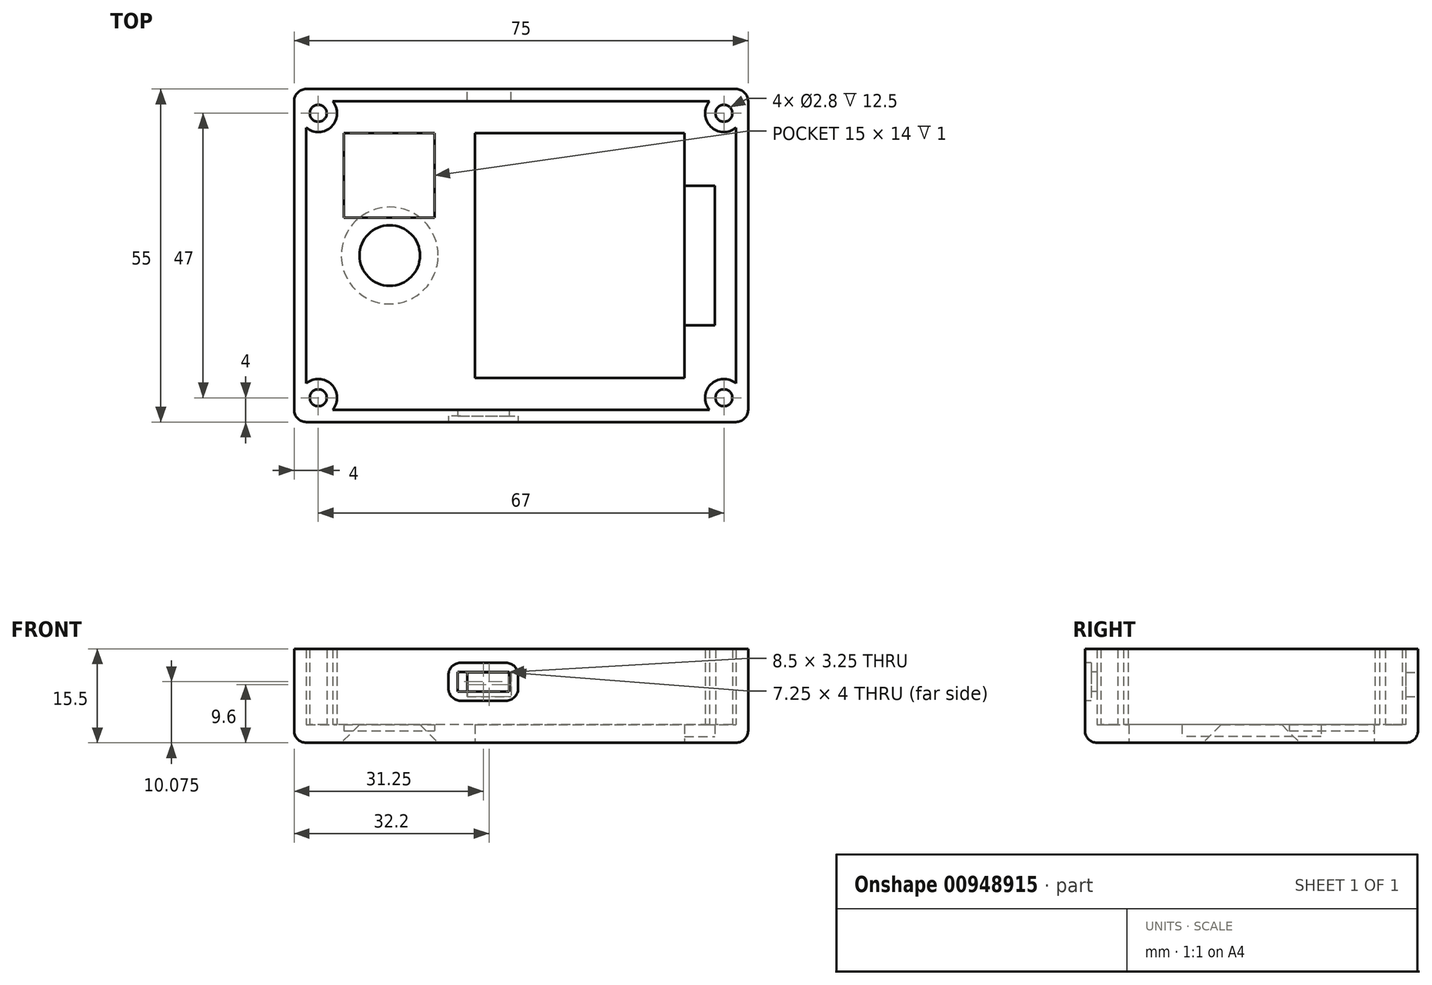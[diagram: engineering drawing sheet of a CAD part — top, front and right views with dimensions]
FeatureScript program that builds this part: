
annotation { "Feature Type Name" : "Feature", "Feature Type Description" : "" }
export const myFeature = defineFeature(function(context is Context, id is Id, definition is map)
    precondition{}
    {
        {
            var Q0;
            Q0=qCreatedBy(makeId("Top.planeOp"),FACE);
            var sketch = newSketch(context, id + "F0", { "sketchPlane" : qUnion([Q0])});
            skLineSegment(sketch, "E0.bottom", {"start": v(35.5, 25.5) * mm, "end": v(-35.5, 25.5) * mm});
            skLineSegment(sketch, "E0.top", {"start": v(35.5, -25.5) * mm, "end": v(-35.5, -25.5) * mm});
            skLineSegment(sketch, "E0.left", {"start": v(35.5, 25.5) * mm, "end": v(35.5, -25.5) * mm});
            skLineSegment(sketch, "E0.right", {"start": v(-35.5, 25.5) * mm, "end": v(-35.5, -25.5) * mm});
            skPoint(sketch, "E0.middle", {"position": v(0, 0) * mm});
            skArc(sketch, "E1", {"start": v(35.5, -21.13) * mm, "mid": v(31.3, -21.3) * mm, "end": v(31.13, -25.5) * mm});
            skArc(sketch, "E2", {"start": v(31.13, -25.5) * mm, "mid": v(35.7, -25.7) * mm, "end": v(35.5, -21.13) * mm, "construction": true});
            skLineSegment(sketch, "E3.bottom", {"start": v(35.5, 27.5) * mm, "end": v(-35.5, 27.5) * mm});
            skLineSegment(sketch, "E3.top", {"start": v(35.5, -27.5) * mm, "end": v(-35.5, -27.5) * mm});
            skLineSegment(sketch, "E3.left", {"start": v(37.5, 25.5) * mm, "end": v(37.5, -25.5) * mm});
            skLineSegment(sketch, "E3.right", {"start": v(-37.5, 25.5) * mm, "end": v(-37.5, -25.5) * mm});
            skArc(sketch, "E4", {"start": v(31.13, 25.5) * mm, "mid": v(31.3, 21.3) * mm, "end": v(35.5, 21.13) * mm});
            skArc(sketch, "E5", {"start": v(35.5, 21.13) * mm, "mid": v(35.7, 25.7) * mm, "end": v(31.13, 25.5) * mm, "construction": true});
            skArc(sketch, "E6", {"start": v(-31.13, 25.5) * mm, "mid": v(-35.7, 25.7) * mm, "end": v(-35.5, 21.13) * mm, "construction": true});
            skArc(sketch, "E7", {"start": v(-35.5, 21.13) * mm, "mid": v(-31.3, 21.3) * mm, "end": v(-31.13, 25.5) * mm});
            skArc(sketch, "E8", {"start": v(-35.5, -21.13) * mm, "mid": v(-35.7, -25.7) * mm, "end": v(-31.13, -25.5) * mm, "construction": true});
            skArc(sketch, "E9", {"start": v(-31.13, -25.5) * mm, "mid": v(-31.3, -21.3) * mm, "end": v(-35.5, -21.13) * mm});
            skPoint(sketch, "E10.visualSharp", {"position": v(37.5, 27.5) * mm});
            skArc(sketch, "E10.filletArc", {"start": v(37.5, 25.5) * mm, "mid": v(36.91, 26.91) * mm, "end": v(35.5, 27.5) * mm});
            skPoint(sketch, "E11.visualSharp", {"position": v(-37.5, 27.5) * mm});
            skArc(sketch, "E11.filletArc", {"start": v(-35.5, 27.5) * mm, "mid": v(-36.91, 26.91) * mm, "end": v(-37.5, 25.5) * mm});
            skPoint(sketch, "E12.visualSharp", {"position": v(-37.5, -27.5) * mm});
            skArc(sketch, "E12.filletArc", {"start": v(-37.5, -25.5) * mm, "mid": v(-36.91, -26.91) * mm, "end": v(-35.5, -27.5) * mm});
            skPoint(sketch, "E13.visualSharp", {"position": v(37.5, -27.5) * mm});
            skArc(sketch, "E13.filletArc", {"start": v(35.5, -27.5) * mm, "mid": v(36.91, -26.91) * mm, "end": v(37.5, -25.5) * mm});
            skLineSegment(sketch, "E14.bottom", {"start": v(-7.6, 20.25) * mm, "end": v(27, 20.25) * mm});
            skLineSegment(sketch, "E14.top", {"start": v(-7.6, -20.25) * mm, "end": v(27, -20.25) * mm});
            skLineSegment(sketch, "E14.left", {"start": v(-7.6, 20.25) * mm, "end": v(-7.6, -20.25) * mm});
            skLineSegment(sketch, "E14.right", {"start": v(27, 20.25) * mm, "end": v(27, -20.25) * mm});
            skPoint(sketch, "E14.middle", {"position": v(9.7, 0) * mm});
            skLineSegment(sketch, "E15.bottom", {"start": v(27, 11.5) * mm, "end": v(32, 11.5) * mm});
            skLineSegment(sketch, "E15.top", {"start": v(27, -11.5) * mm, "end": v(32, -11.5) * mm});
            skLineSegment(sketch, "E15.left", {"start": v(27, 11.5) * mm, "end": v(27, -11.5) * mm});
            skLineSegment(sketch, "E15.right", {"start": v(32, 11.5) * mm, "end": v(32, -11.5) * mm});
            skPoint(sketch, "E15.middle", {"position": v(29.5, 0) * mm});
            skCircle(sketch, "E16", {"center": v(-21.7, 0) * mm, "radius": 5 * mm});
            skCircle(sketch, "E17", {"center": v(-33.5, 23.5) * mm, "radius": 1.4 * mm});
            skCircle(sketch, "E18", {"center": v(33.5, 23.5) * mm, "radius": 1.4 * mm});
            skCircle(sketch, "E19", {"center": v(33.5, -23.5) * mm, "radius": 1.4 * mm});
            skCircle(sketch, "E20", {"center": v(-33.5, -23.5) * mm, "radius": 1.4 * mm});
            skLineSegment(sketch, "E21.MirrorCS", {"start": v(-29.3, 6.25) * mm, "end": v(-29.3, 20.25) * mm});
            skLineSegment(sketch, "E22.MirrorCS", {"start": v(-29.3, 6.25) * mm, "end": v(-14.3, 6.25) * mm});
            skLineSegment(sketch, "E23.MirrorCS", {"start": v(-14.3, 6.25) * mm, "end": v(-14.3, 20.25) * mm});
            skLineSegment(sketch, "E24.MirrorCS", {"start": v(-29.3, 20.25) * mm, "end": v(-14.3, 20.25) * mm});
            skSolve(sketch);
        }
        {
            var Q0;
            Q0=makeQuery(id+"F0.imprint","IMPRINT",FACE,{"disambiguationData":[TD([[makeQuery(id+"F0.imprint","IMPRINT",EDGE,{"derivedFrom":sQuery(id+"F0.wireOp",EDGE,"WyYnpZns-yAxv-1ikW-t9UI-voqzsf8WS2MO.top")}),-1.0]])]});
            var Q1;
            {var subQ0=sQuery(id+"F0.wireOp",EDGE,"WyYnpZns-yAxv-1ikW-t9UI-voqzsf8WS2MO.bottom");Q1=makeQuery(id+"F0.imprint","IMPRINT",FACE,{"disambiguationData":[TD([[makeQuery(id+"F0.imprint","IMPRINT",EDGE,{"derivedFrom":subQ0}),1.0]])]});}
            var Q2;
            {var subQ3=sQuery(id+"F0.wireOp",EDGE,"E1");Q2=makeQuery(id+"F0.imprint","IMPRINT",FACE,{"disambiguationData":[TD([[makeQuery(id+"F0.imprint","IMPRINT",EDGE,{"derivedFrom":subQ3}),-1.0]])]});}
            var Q3;
            Q3=makeQuery(id+"F0.imprint","IMPRINT",FACE,{"disambiguationData":[TD([[makeQuery(id+"F0.imprint","IMPRINT",EDGE,{"derivedFrom":sQuery(id+"F0.wireOp",EDGE,"eHnNjm3S-WHwl-CNDd-T52B-1u3afqCrOUJR.bottom")}),-1.0]])]});
            extrude(context, id + "F1", {"entities" : qUnion([Q0, Q1, Q2, Q3]), "depth" : 3 * mm, "offsetDistance" : 25 * mm});
        }
        {
            var Q0;
            Q0=makeQuery(id+"F0.imprint","IMPRINT",FACE,{"disambiguationData":[TD([[makeQuery(id+"F0.imprint","IMPRINT",EDGE,{"derivedFrom":sQuery(id+"F0.wireOp",EDGE,"eHnNjm3S-WHwl-CNDd-T52B-1u3afqCrOUJR.bottom")}),-1.0]])]});
            var Q1;
            {var subQ0=sQuery(id+"F0.wireOp",EDGE,"E15.bottom");Q1=makeQuery(id+"F0.imprint","IMPRINT",FACE,{"disambiguationData":[TD([[makeQuery(id+"F0.imprint","IMPRINT",EDGE,{"derivedFrom":subQ0}),-1.0]])]});}
            var Q2;
            {var subQ0=sQuery(id+"F0.wireOp",EDGE,"WyYnpZns-yAxv-1ikW-t9UI-voqzsf8WS2MO.bottom");Q2=makeQuery(id+"F0.imprint","IMPRINT",FACE,{"disambiguationData":[TD([[makeQuery(id+"F0.imprint","IMPRINT",EDGE,{"derivedFrom":subQ0}),-1.0]])]});}
            extrude(context, id + "F2", {"entities" : qUnion([Q0, Q1, Q2]), "operationType" : NewBodyOperationType.ADD, "depth" : 1 * mm, "offsetDistance" : 25 * mm});
        }
        {
            var Q0;
            Q0=makeQuery(id+"F0.imprint","IMPRINT",FACE,{"disambiguationData":[TD([[makeQuery(id+"F0.imprint","IMPRINT",EDGE,{"derivedFrom":sQuery(id+"F0.wireOp",EDGE,"E3.bottom")}),1.0]])]});
            var Q1;
            {var subQ3=sQuery(id+"F0.wireOp",EDGE,"E7");Q1=makeQuery(id+"F0.imprint","IMPRINT",FACE,{"disambiguationData":[TD([[makeQuery(id+"F0.imprint","IMPRINT",EDGE,{"derivedFrom":subQ3}),1.0]])]});}
            var Q2;
            {var subQ0=sQuery(id+"F0.wireOp",EDGE,"E9");Q2=makeQuery(id+"F0.imprint","IMPRINT",FACE,{"disambiguationData":[TD([[makeQuery(id+"F0.imprint","IMPRINT",EDGE,{"derivedFrom":subQ0}),1.0]])]});}
            var Q3;
            {var subQ0=sQuery(id+"F0.wireOp",EDGE,"E1");Q3=makeQuery(id+"F0.imprint","IMPRINT",FACE,{"disambiguationData":[TD([[makeQuery(id+"F0.imprint","IMPRINT",EDGE,{"derivedFrom":subQ0}),1.0]])]});}
            var Q4;
            {var subQ0=sQuery(id+"F0.wireOp",EDGE,"E4");Q4=makeQuery(id+"F0.imprint","IMPRINT",FACE,{"disambiguationData":[TD([[makeQuery(id+"F0.imprint","IMPRINT",EDGE,{"derivedFrom":subQ0}),1.0]])]});}
            extrude(context, id + "F3", {"entities" : qUnion([Q0, Q1, Q2, Q3, Q4]), "operationType" : NewBodyOperationType.ADD, "depth" : 15.5 * mm, "offsetDistance" : 25 * mm});
        }
        {
            var Q0;
            Q0=makeQuery(id+"F0.imprint","IMPRINT",FACE,{"disambiguationData":[TD([[makeQuery(id+"F0.imprint","IMPRINT",EDGE,{"derivedFrom":sQuery(id+"F0.wireOp",EDGE,"E19")}),1.0]])]});
            var Q1;
            Q1=makeQuery(id+"F0.imprint","IMPRINT",FACE,{"disambiguationData":[TD([[makeQuery(id+"F0.imprint","IMPRINT",EDGE,{"derivedFrom":sQuery(id+"F0.wireOp",EDGE,"E18")}),1.0]])]});
            var Q2;
            Q2=makeQuery(id+"F0.imprint","IMPRINT",FACE,{"disambiguationData":[TD([[makeQuery(id+"F0.imprint","IMPRINT",EDGE,{"derivedFrom":sQuery(id+"F0.wireOp",EDGE,"E17")}),1.0]])]});
            var Q3;
            Q3=makeQuery(id+"F0.imprint","IMPRINT",FACE,{"disambiguationData":[TD([[makeQuery(id+"F0.imprint","IMPRINT",EDGE,{"derivedFrom":sQuery(id+"F0.wireOp",EDGE,"E20")}),1.0]])]});
            extrude(context, id + "F4", {"entities" : qUnion([Q0, Q1, Q2, Q3]), "operationType" : NewBodyOperationType.ADD, "depth" : 3 * mm, "offsetDistance" : 25 * mm});
        }
        {
            var Q0;
            Q0=makeQuery(id+"F3.opExtrude","CAP_EDGE",EDGE,{"disambiguationData":[OSD([sQuery(id+"F0.wireOp",EDGE,"E3.right")])],"isStart":true});
            fillet(context, id + "F5", {"entities" : qUnion([Q0]), "radius" : 2 * mm, "tangentPropagation" : true, "allowEdgeOverflow" : false});
        }
        {
            var Q0;
            Q0=makeQuery(id+"F3.opExtrude","SWEPT_FACE",FACE,{"disambiguationData":[OSD([sQuery(id+"F0.wireOp",EDGE,"E3.bottom")])]});
            var sketch = newSketch(context, id + "F6", { "sketchPlane" : qUnion([Q0])});
            skLineSegment(sketch, "E25.bottom", {"start": v(1.67, 7.6) * mm, "end": v(8.92, 7.6) * mm});
            skLineSegment(sketch, "E25.top", {"start": v(1.67, 11.6) * mm, "end": v(8.92, 11.6) * mm});
            skLineSegment(sketch, "E25.left", {"start": v(1.67, 7.6) * mm, "end": v(1.67, 11.6) * mm});
            skLineSegment(sketch, "E25.right", {"start": v(8.92, 7.6) * mm, "end": v(8.92, 11.6) * mm});
            skPoint(sketch, "E25.middle", {"position": v(5.3, 9.6) * mm});
            skSolve(sketch);
        }
        {
            var Q0;
            Q0=makeQuery(id+"F6.imprint","IMPRINT",FACE,{"disambiguationData":[TD([[makeQuery(id+"F6.imprint","IMPRINT",EDGE,{"derivedFrom":sQuery(id+"F6.wireOp",EDGE,"E25.bottom")}),1.0]])]});
            extrude(context, id + "F7", {"entities" : qUnion([Q0]), "operationType" : NewBodyOperationType.REMOVE, "oppositeDirection" : true, "depth" : 25 * mm, "offsetDistance" : 25 * mm});
        }
        {
            var Q0;
            Q0=makeQuery(id+"F3.opExtrude","SWEPT_FACE",FACE,{"disambiguationData":[OSD([sQuery(id+"F0.wireOp",EDGE,"E3.top")])]});
            var sketch = newSketch(context, id + "F8", { "sketchPlane" : qUnion([Q0])});
            skLineSegment(sketch, "E26.bottom", {"start": v(-10.5, 11.7) * mm, "end": v(-2, 11.7) * mm});
            skLineSegment(sketch, "E26.top", {"start": v(-10.5, 8.45) * mm, "end": v(-2, 8.45) * mm});
            skLineSegment(sketch, "E26.left", {"start": v(-10.5, 11.7) * mm, "end": v(-10.5, 8.45) * mm});
            skLineSegment(sketch, "E26.right", {"start": v(-2, 11.7) * mm, "end": v(-2, 8.45) * mm});
            skLineSegment(sketch, "E27.bottom", {"start": v(-12, 13.2) * mm, "end": v(-0.5, 13.2) * mm});
            skLineSegment(sketch, "E27.top", {"start": v(-12, 6.95) * mm, "end": v(-0.5, 6.95) * mm});
            skLineSegment(sketch, "E27.left", {"start": v(-12, 13.2) * mm, "end": v(-12, 6.95) * mm});
            skLineSegment(sketch, "E27.right", {"start": v(-0.5, 13.2) * mm, "end": v(-0.5, 6.95) * mm});
            skSolve(sketch);
        }
        {
            var Q0;
            Q0=makeQuery(id+"F8.imprint","IMPRINT",FACE,{"disambiguationData":[TD([[makeQuery(id+"F8.imprint","IMPRINT",EDGE,{"derivedFrom":sQuery(id+"F8.wireOp",EDGE,"E26.bottom")}),-1.0]])]});
            extrude(context, id + "F9", {"entities" : qUnion([Q0]), "operationType" : NewBodyOperationType.REMOVE, "oppositeDirection" : true, "depth" : 25 * mm, "offsetDistance" : 25 * mm});
        }
        {
            var Q0;
            Q0=makeQuery(id+"F8.imprint","IMPRINT",FACE,{"disambiguationData":[TD([[makeQuery(id+"F8.imprint","IMPRINT",EDGE,{"derivedFrom":sQuery(id+"F8.wireOp",EDGE,"E26.bottom")}),1.0]])]});
            extrude(context, id + "F10", {"entities" : qUnion([Q0]), "operationType" : NewBodyOperationType.REMOVE, "oppositeDirection" : true, "depth" : 1 * mm, "offsetDistance" : 25 * mm});
        }
        {
            var Q0;
            Q0=makeQuery(id+"F10.boolean.opBoolean","COPY",EDGE,{"derivedFrom":makeQuery(id+"F10.opExtrude","SWEPT_EDGE",EDGE,{"disambiguationData":[OSD([sQuery(id+"F8.wireOp",EDGE,"E27.bottom"),sQuery(id+"F8.wireOp",EDGE,"E27.right")])]})});
            var Q1;
            Q1=makeQuery(id+"F10.boolean.opBoolean","COPY",EDGE,{"derivedFrom":makeQuery(id+"F10.opExtrude","SWEPT_EDGE",EDGE,{"disambiguationData":[OSD([sQuery(id+"F8.wireOp",EDGE,"E27.top"),sQuery(id+"F8.wireOp",EDGE,"E27.right")])]})});
            var Q2;
            Q2=makeQuery(id+"F10.boolean.opBoolean","COPY",EDGE,{"derivedFrom":makeQuery(id+"F10.opExtrude","SWEPT_EDGE",EDGE,{"disambiguationData":[OSD([sQuery(id+"F8.wireOp",EDGE,"E27.top"),sQuery(id+"F8.wireOp",EDGE,"E27.left")])]})});
            var Q3;
            Q3=makeQuery(id+"F10.boolean.opBoolean","COPY",EDGE,{"derivedFrom":makeQuery(id+"F10.opExtrude","SWEPT_EDGE",EDGE,{"disambiguationData":[OSD([sQuery(id+"F8.wireOp",EDGE,"E27.bottom"),sQuery(id+"F8.wireOp",EDGE,"E27.left")])]})});
            fillet(context, id + "F11", {"entities" : qUnion([Q0, Q1, Q2, Q3]), "radius" : 2 * mm, "tangentPropagation" : true, "allowEdgeOverflow" : false});
        }
        {
            var Q0;
            Q0=makeQuery(id+"F0.imprint","IMPRINT",FACE,{"disambiguationData":[TD([[makeQuery(id+"F0.imprint","IMPRINT",EDGE,{"derivedFrom":sQuery(id+"F0.wireOp",EDGE,"E21.MirrorCS")}),-1.0]])]});
            extrude(context, id + "F12", {"entities" : qUnion([Q0]), "operationType" : NewBodyOperationType.ADD, "depth" : 2 * mm, "offsetDistance" : 25 * mm});
        }
        {
            var Q0;
            Q0=makeQuery(id+"F1.opExtrude","CAP_EDGE",EDGE,{"disambiguationData":[OSD([sQuery(id+"F0.wireOp",EDGE,"E16")])],"isStart":true});
            chamfer(context, id + "F13", {"entities" : qUnion([Q0]), "width" : 3 * mm, "tangentPropagation" : true});
        }
    });
